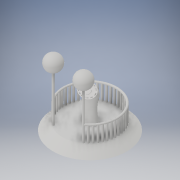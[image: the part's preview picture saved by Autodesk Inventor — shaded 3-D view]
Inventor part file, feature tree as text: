
AUTODESK INVENTOR PART (.ipt)
format: ipt  version: 2017 (Build 210142000, 142)  size: 1,376,768 bytes
history: native  units: in
note: dims shown in document units (in); Inventor stores cm internally (conversion verified against a paired STEP export)
features: other x22, loft x16, sketch x13, extrude x7, plane x1, fillet x1
ambient origin geometry x8: Origin, YZ Plane, XZ Plane, XY Plane, X Axis, Y Axis, Z Axis, Center Point
bodies: Body1 (feature_tree), Body2 (feature_tree)
feature tree (60):
  other  "bace + terminal"
  other  "bace of terminal"
  other  "middle workplane"
  other  "middle"
  other  "top workplane"
  loft  "curved tower"
  other  "pivit point for face of terminal"
  other  "Work Axis1"
  other  "terminal curve"
  other  "face of terminal"
  loft  "terminal face out"
  sketch  "Sketch10"  dims[d2=2.0in d3=0.8in]
  plane  "Work Plane7"
  sketch  "Sketch11"  dims[d4=0.55in d5=1.0in]
  loft  "terminal hole 1"
  loft  "terminal hole 2"
  loft  "terminal hole 3"
  loft  "terminal hole 4"
  loft  "terminal hole 5"
  loft  "terminal hole 6"
  loft  "terminal hole 7"
  loft  "terminal hole 8"
  loft  "terminal hole 9"
  loft  "terminal hole 10"
  loft  "terminal hole 11"
  loft  "terminal hole 12"
  loft  "terminal hole 13"
  loft  "terminal hole 14"
  fillet  "cuved edjes on termanal face"  [1 undecoded]
  extrude  "back hole for button"  TaperAngle=0.0deg  [1 undecoded]
  extrude  "side gap"  TaperAngle=0.0deg  [1 undecoded]
  extrude  "button"  TaperAngle=0.0deg  [1 undecoded]
  extrude  "bace"  TaperAngle=0.0deg  [1 undecoded]
  other  "ramp around"
  extrude  "railing bars"  TaperAngle=0.0deg  [1 undecoded]
  other  "railing bar top workplane"
  other  "railing bar top"
  extrude  "light pole"  TaperAngle=0.0deg  [1 undecoded]
  other  "globe light workplane"
  sketch  "Sketch20"  dims[d39=-0.2in]
  other  "light 1"
  other  "light 2"
  extrude  "line up slot"  TaperAngle=0.0deg  [1 undecoded]
  other  "top"
  sketch  "Sketch8"  dims[d0=1.0in d1=0.75in]
  other  "Edges1"
  sketch  "Sketch12"  dims[d6=0.75in d7=1.0in]
  sketch  "Sketch13"  dims[d8=0.0in d9=90.0deg d10=0.0in d11=90.0deg d12=0.0in d13=90.0deg d16=45.0deg]
  sketch  "Sketch14"  dims[d18=0.2in d19=1.2in]
  other  "terminal button"
  sketch  "Sketch15"  dims[d20=0.85in d21=0.0in d22=90.0deg]
  sketch  "Sketch16"  dims[d23=0.0in d24=90.0deg d27=1.1in]
  sketch  "Sketch17"  dims[d28=0.75in d29=1.0in]
  other  "Work Axis3"
  other  "Work Axis4"
  sketch  "Sketch18"  dims[d30=0.65in d33=0.0481in]
  sketch  "Sketch19"  dims[d34=0.0481in d35=5.5118in d37=360.0deg]
  other  "Work Axis5"
  other  "Work Axis6"
  sketch  "Sketch21"  dims[d41=5.5118in d42=1.1in d43=0.85in d44=1.0in d45=0.75in d46=0.0481in d47=0.0481in d48=360.0deg d49=1.2in d50=0.85in d51=1.0in d52=0.75in d53=0.0in d54=90.0deg d55=0.0in d56=90.0deg d57=0.0in d58=90.0deg d59=0.0in d60=90.0deg d61=0.0in d62=90.0deg d63=0.0in d64=90.0deg d65=0.0in d66=90.0deg d67=0.0in d68=90.0deg d69=0.0in d70=90.0deg d71=0.0in d72=90.0deg d73=0.0in d74=90.0deg d75=0.0in d76=90.0deg d77=0.0in d78=90.0deg d79=0.0in d80=90.0deg d81=0.0in d82=90.0deg d83=0.0in d84=90.0deg d85=0.0in d86=90.0deg d87=0.0in d88=90.0deg d89=0.0in d90=90.0deg d91=0.0in d92=90.0deg d93=0.0in d94=90.0deg d95=0.0in d96=90.0deg d97=0.0in d98=90.0deg d99=0.0in d100=90.0deg d105=0.0in d106=90.0deg d107=0.0in d108=90.0deg d109=0.0in d110=90.0deg d111=0.0in d112=90.0deg d113=0.01in d114=1.0in d115=0.1in d116=0.0in d117=1.1in d118=0.05in d119=0.0in d120=0.05in d121=0.0in d122=7.0in d123=1.0in d124=0.0in d134=0.7579in d135=15.748in d137=1.9948in d139=2.0in d140=0.0in d141=0.2749in d142=90.0deg d143=0.25in d144=0.25in d145=90.0deg d146=4.0in d147=0.0in d150=2.0in d151=0.9in d152=2.0in d153=0.9in d155=90.0deg d156=90.0deg d157=0.0in d158=2.0in d159=0.2in d160=0.0in]
note: 8 required parameter values undecoded (feature->parameter linkage not recoverable at this tier; creation-order binding heuristic only, values carry confidence <= 0.55)
